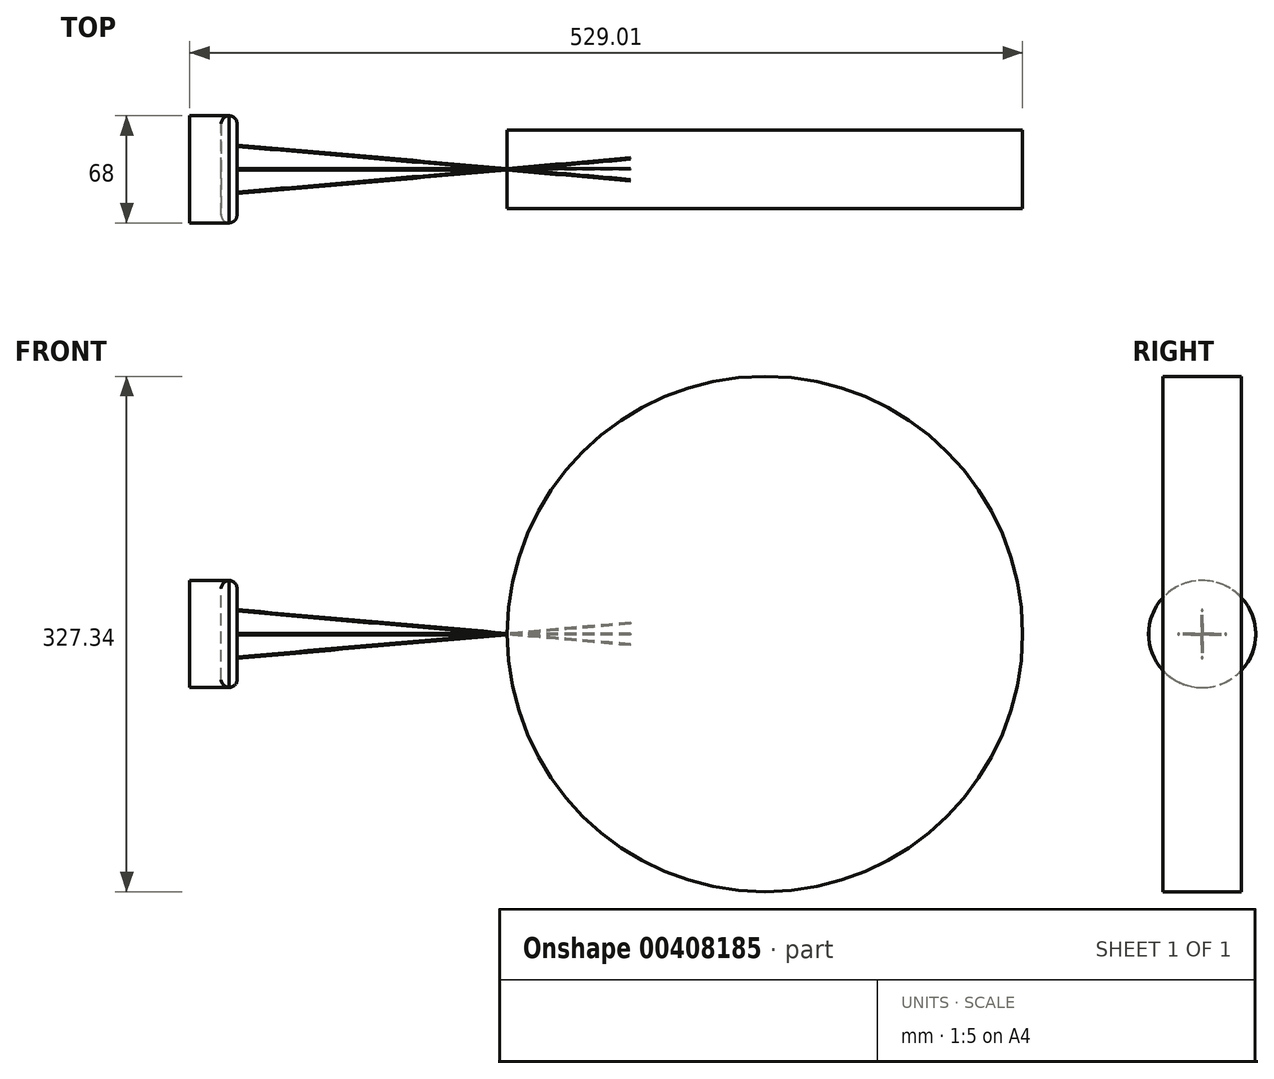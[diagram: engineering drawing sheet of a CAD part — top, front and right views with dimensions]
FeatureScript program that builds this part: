
annotation { "Feature Type Name" : "Feature", "Feature Type Description" : "" }
export const myFeature = defineFeature(function(context is Context, id is Id, definition is map)
    precondition{}
    {
        {
            var Q0;
            Q0=qCreatedBy(makeId("Right.planeOp"),FACE);
            var sketch = newSketch(context, id + "F0", { "sketchPlane" : qUnion([Q0])});
            skCircle(sketch, "E0", {"center": v(0, 15) * mm, "radius": 0.5 * mm});
            skSolve(sketch);
        }
        {
            var Q0;
            Q0=qCreatedBy(makeId("Right.planeOp"),FACE);
            var sketch = newSketch(context, id + "F1", { "sketchPlane" : qUnion([Q0])});
            skCircle(sketch, "E1", {"center": v(0, 0) * mm, "radius": 34 * mm});
            skSolve(sketch);
        }
        {
            var Q0;
            Q0=qCreatedBy(makeId("Front.planeOp"),FACE);
            var sketch = newSketch(context, id + "F2", { "sketchPlane" : qUnion([Q0])});
            skLineSegment(sketch, "E2", {"start": v(0, 15) * mm, "end": v(250, -6.87) * mm});
            skSolve(sketch);
        }
        {
            var Q0;
            Q0 = qSketchRegion(id + "F0", true);
            var Q1;
            Q1=sQuery(id+"F2.wireOp",EDGE,"E2");
            sweep(context, id + "F3", {"profiles" : qUnion([Q0]), "path" : qUnion([Q1])});
        }
        {
            var Q0;
            Q0=qCreatedBy(makeId("Front.planeOp"),FACE);
            var sketch = newSketch(context, id + "F4", { "sketchPlane" : qUnion([Q0])});
            skLineSegment(sketch, "E3", {"start": v(0, 0) * mm, "end": v(300, 0) * mm});
            skSolve(sketch);
        }
        {
            var Q0;
            Q0=makeQuery(id+"F3.opSweep","SWEPT_BODY",BODY,{"disambiguationData":[OSD([sQuery(id+"F0.wireOp",EDGE,"E0"),sQuery(id+"F2.wireOp",EDGE,"E2")])]});
            var Q1;
            Q1=sQuery(id+"F4.wireOp",EDGE,"E3");
            circularPattern(context, id + "F5", {"entities" : qUnion([Q0]), "axis" : qUnion([Q1]), "angle" : 360 * degree, "instanceCount" : 4, "equalSpace" : true});
        }
        {
            var Q0;
            Q0=makeQuery(id+"F1.imprint","IMPRINT",FACE,{"disambiguationData":[TD([[makeQuery(id+"F1.imprint","IMPRINT",EDGE,{"derivedFrom":sQuery(id+"F1.wireOp",EDGE,"E1")}),1.0]])]});
            var Q1;
            Q1=sQuery(id+"F1.wireOp",EDGE,"E1");
            extrude(context, id + "F6", {"entities" : qUnion([Q0]), "surfaceEntities" : qUnion([Q1]), "oppositeDirection" : true, "depth" : 10 * mm});
        }
        {
            var Q0;
            Q0=makeQuery(id+"F6.opExtrude","CAP_EDGE",EDGE,{"disambiguationData":[OSD([sQuery(id+"F1.wireOp",EDGE,"E1")])],"isStart":true});
            var Q1;
            Q1=makeQuery(id+"F6.opExtrude","CAP_EDGE",EDGE,{"disambiguationData":[OSD([sQuery(id+"F1.wireOp",EDGE,"E1")])],"isStart":false});
            fillet(context, id + "F7", {"entities" : qUnion([Q0, Q1]), "radius" : 5 * mm, "tangentPropagation" : true, "allowEdgeOverflow" : false});
        }
        {
            var Q0;
            Q0=qCreatedBy(makeId("Right.planeOp"),FACE);
            cPlane(context, id + "F8", {"entities" : qUnion([Q0]), "cplaneType" : CPlaneType.OFFSET, "offset" : 5 * mm, "oppositeDirection" : true, "width" : 150 * mm, "height" : 150 * mm});
        }
        {
            var Q0;
            Q0=qCreatedBy(id+"F8.planeOp",FACE);
            var sketch = newSketch(context, id + "F9", { "sketchPlane" : qUnion([Q0])});
            skCircle(sketch, "E4", {"center": v(0, 0) * mm, "radius": 34 * mm});
            skSolve(sketch);
        }
        {
            var Q0;
            Q0 = qSketchRegion(id + "F9", true);
            extrude(context, id + "F10", {"entities" : qUnion([Q0]), "oppositeDirection" : true, "depth" : 25 * mm});
        }
        {
            var Q0;
            Q0=qCreatedBy(makeId("Front.planeOp"),FACE);
            var sketch = newSketch(context, id + "F11", { "sketchPlane" : qUnion([Q0])});
            skCircle(sketch, "E5", {"center": v(335.33, 0) * mm, "radius": 163.67 * mm});
            skSolve(sketch);
        }
        {
            var Q0;
            Q0 = qSketchRegion(id + "F11", true);
            extrude(context, id + "F12", {"entities" : qUnion([Q0]), "depth" : 25 * mm, "offsetDistance" : 25 * mm, "hasSecondDirection" : true, "secondDirectionOppositeDirection" : true, "secondDirectionDepth" : 25 * mm});
        }
    });
